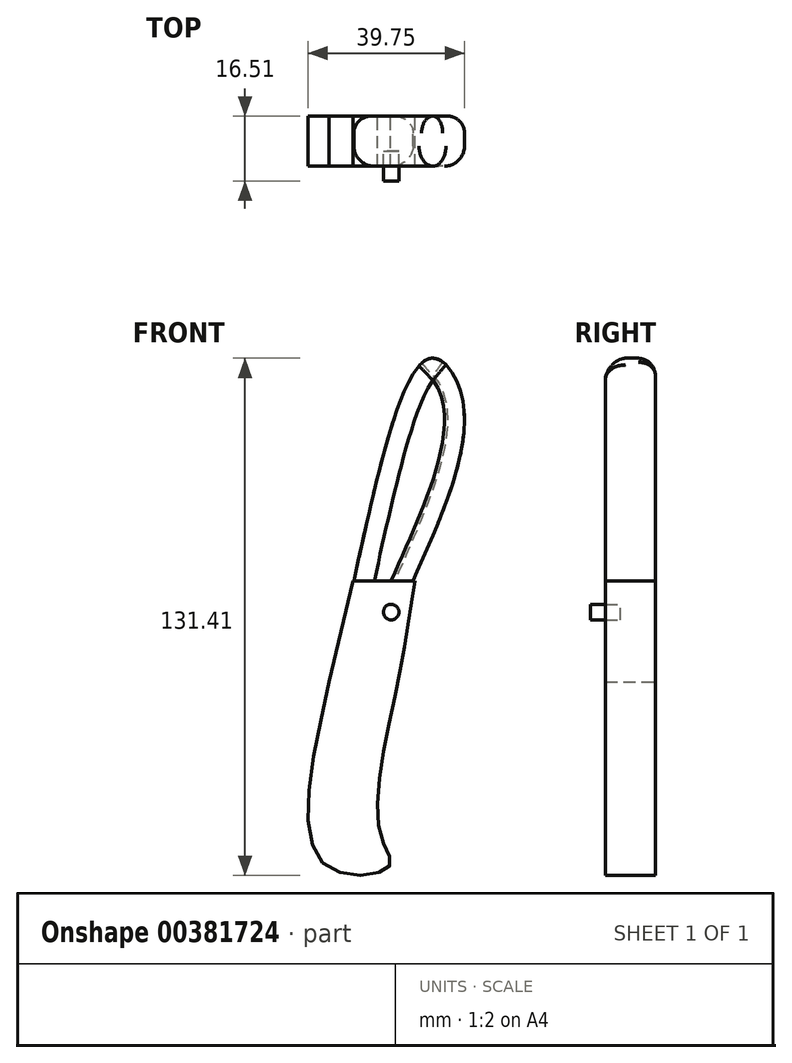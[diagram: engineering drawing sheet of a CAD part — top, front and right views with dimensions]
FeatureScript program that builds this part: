
annotation { "Feature Type Name" : "Feature", "Feature Type Description" : "" }
export const myFeature = defineFeature(function(context is Context, id is Id, definition is map)
    precondition{}
    {
        {
            var Q0;
            Q0=qCreatedBy(makeId("Front.planeOp"),FACE);
            var sketch = newSketch(context, id + "F0", { "sketchPlane" : qUnion([Q0])});
            skFitSpline(sketch, "E0", {"points": [v(-25.63, -25.72) * mm, v(-26.4, -72.41) * mm, v(-10.4, -72.67) * mm, v(-12.69, -64.04) * mm, v(-8.88, -29.27) * mm, v(-3.8, 0) * mm], "startDerivative": vector(-49.9, -223.03) * mm, "endDerivative": vector(19.28, 125.9) * mm});
            skFitSpline(sketch, "E1", {"points": [v(-25.63, -25.72) * mm, v(-19.54, 0) * mm], "startDerivative": vector(6.1, 25.72) * mm, "endDerivative": vector(6.1, 25.72) * mm});
            skLineSegment(sketch, "E2", {"start": v(-19.54, 0) * mm, "end": v(-3.8, 0) * mm});
            skSolve(sketch);
        }
        {
            var Q0;
            Q0=qCreatedBy(makeId("Front.planeOp"),FACE);
            var sketch = newSketch(context, id + "F1", { "sketchPlane" : qUnion([Q0])});
            skFitSpline(sketch, "E3", {"points": [v(-4.3, 0) * mm, v(8.45, 45) * mm, v(0, 56.48) * mm, v(-19.34, 0) * mm], "startDerivative": vector(58.9, 131.91) * mm, "endDerivative": vector(-42.96, -195.76) * mm});
            skLineSegment(sketch, "E4", {"start": v(-19.34, 0) * mm, "end": v(-4.3, 0) * mm});
            skSolve(sketch);
        }
        {
            var Q0;
            Q0 = qSketchRegion(id + "F0", true);
            extrude(context, id + "F2", {"entities" : qUnion([Q0]), "depth" : 12.7 * mm});
        }
        {
            var Q0;
            Q0 = qSketchRegion(id + "F1", true);
            extrude(context, id + "F3", {"entities" : qUnion([Q0]), "depth" : 12.7 * mm});
        }
        {
            var Q0;
            Q0=makeQuery(id+"F3.opExtrude","CAP_EDGE",EDGE,{"disambiguationData":[OSD([sQuery(id+"F1.wireOp",EDGE,"E3")])],"isStart":false});
            fillet(context, id + "F4", {"entities" : qUnion([Q0]), "radius" : 5.08 * mm, "tangentPropagation" : true, "allowEdgeOverflow" : false});
        }
        {
            var Q0;
            Q0=makeQuery(id+"F3.opExtrude","CAP_EDGE",EDGE,{"disambiguationData":[OSD([sQuery(id+"F1.wireOp",EDGE,"E3")])],"isStart":true});
            fillet(context, id + "F5", {"entities" : qUnion([Q0]), "radius" : 4.3 * mm, "tangentPropagation" : true, "allowEdgeOverflow" : false});
        }
        {
            var Q0;
            Q0=makeQuery(id+"F2.opExtrude","CAP_FACE",FACE,{"disambiguationData":[OSD([sQuery(id+"F0.wireOp",EDGE,"E0"),sQuery(id+"F0.wireOp",EDGE,"E1"),sQuery(id+"F0.wireOp",EDGE,"E2")])],"isStart":false});
            var sketch = newSketch(context, id + "F6", { "sketchPlane" : qUnion([Q0])});
            skCircle(sketch, "E5", {"center": v(-9.86, -7.96) * mm, "radius": 1.97 * mm});
            skSolve(sketch);
        }
        {
            var Q0;
            Q0 = qSketchRegion(id + "F6", true);
            extrude(context, id + "F7", {"entities" : qUnion([Q0]), "endBound" : BoundingType.SYMMETRIC, "depth" : 7.62 * mm});
        }
    });
